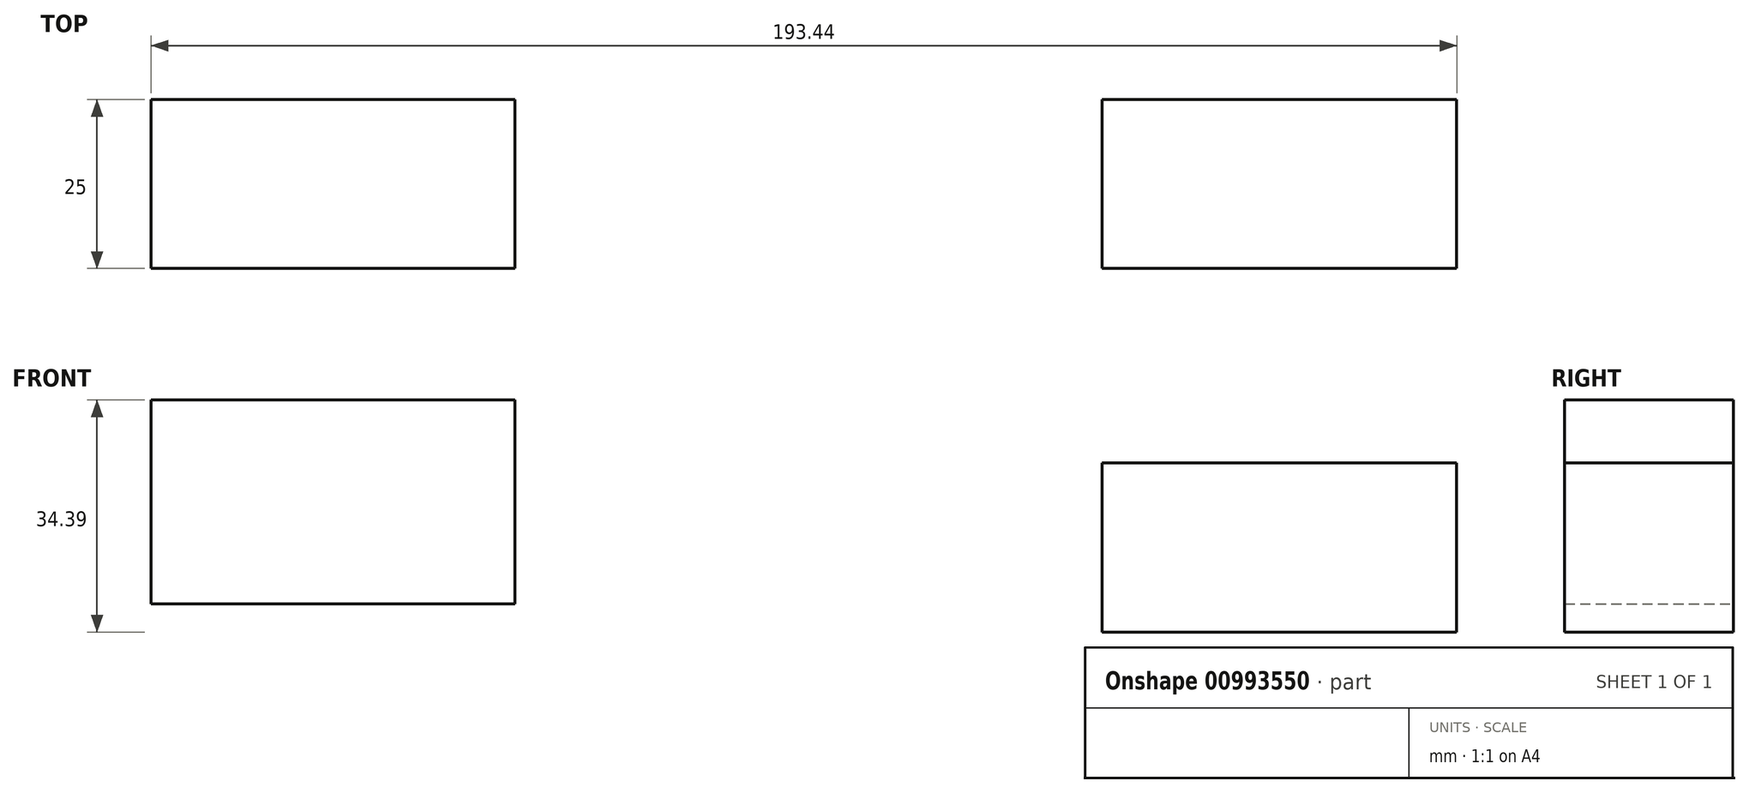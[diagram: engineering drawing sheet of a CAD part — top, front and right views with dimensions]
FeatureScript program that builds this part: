
annotation { "Feature Type Name" : "Feature", "Feature Type Description" : "" }
export const myFeature = defineFeature(function(context is Context, id is Id, definition is map)
    precondition{}
    {
        {
            var Q0;
            Q0=qCreatedBy(makeId("Front.planeOp"),FACE);
            var sketch = newSketch(context, id + "F0", { "sketchPlane" : qUnion([Q0])});
            skLineSegment(sketch, "E0.bottom", {"start": v(-126.74, 14.2) * mm, "end": v(-72.86, 14.2) * mm});
            skLineSegment(sketch, "E0.top", {"start": v(-126.74, -16) * mm, "end": v(-72.86, -16) * mm});
            skLineSegment(sketch, "E0.left", {"start": v(-126.74, 14.2) * mm, "end": v(-126.74, -16) * mm});
            skLineSegment(sketch, "E0.right", {"start": v(-72.86, 14.2) * mm, "end": v(-72.86, -16) * mm});
            skLineSegment(sketch, "E1.bottom", {"start": v(14.12, 4.89) * mm, "end": v(66.7, 4.89) * mm});
            skLineSegment(sketch, "E1.top", {"start": v(14.12, -20.18) * mm, "end": v(66.7, -20.18) * mm});
            skLineSegment(sketch, "E1.left", {"start": v(14.12, 4.89) * mm, "end": v(14.12, -20.18) * mm});
            skLineSegment(sketch, "E1.right", {"start": v(66.7, 4.89) * mm, "end": v(66.7, -20.18) * mm});
            skSolve(sketch);
        }
        {
            var Q0;
            Q0=makeQuery(id+"F0.imprint","IMPRINT",FACE,{"disambiguationData":[TD([[makeQuery(id+"F0.imprint","IMPRINT",EDGE,{"derivedFrom":sQuery(id+"F0.wireOp",EDGE,"E1.bottom")}),-1.0]])]});
            var Q1;
            Q1=makeQuery(id+"F0.imprint","IMPRINT",FACE,{"disambiguationData":[TD([[makeQuery(id+"F0.imprint","IMPRINT",EDGE,{"derivedFrom":sQuery(id+"F0.wireOp",EDGE,"E0.bottom")}),-1.0]])]});
            extrude(context, id + "F1", {"entities" : qUnion([Q0, Q1]), "depth" : 25 * mm, "offsetDistance" : 25 * mm});
        }
    });
